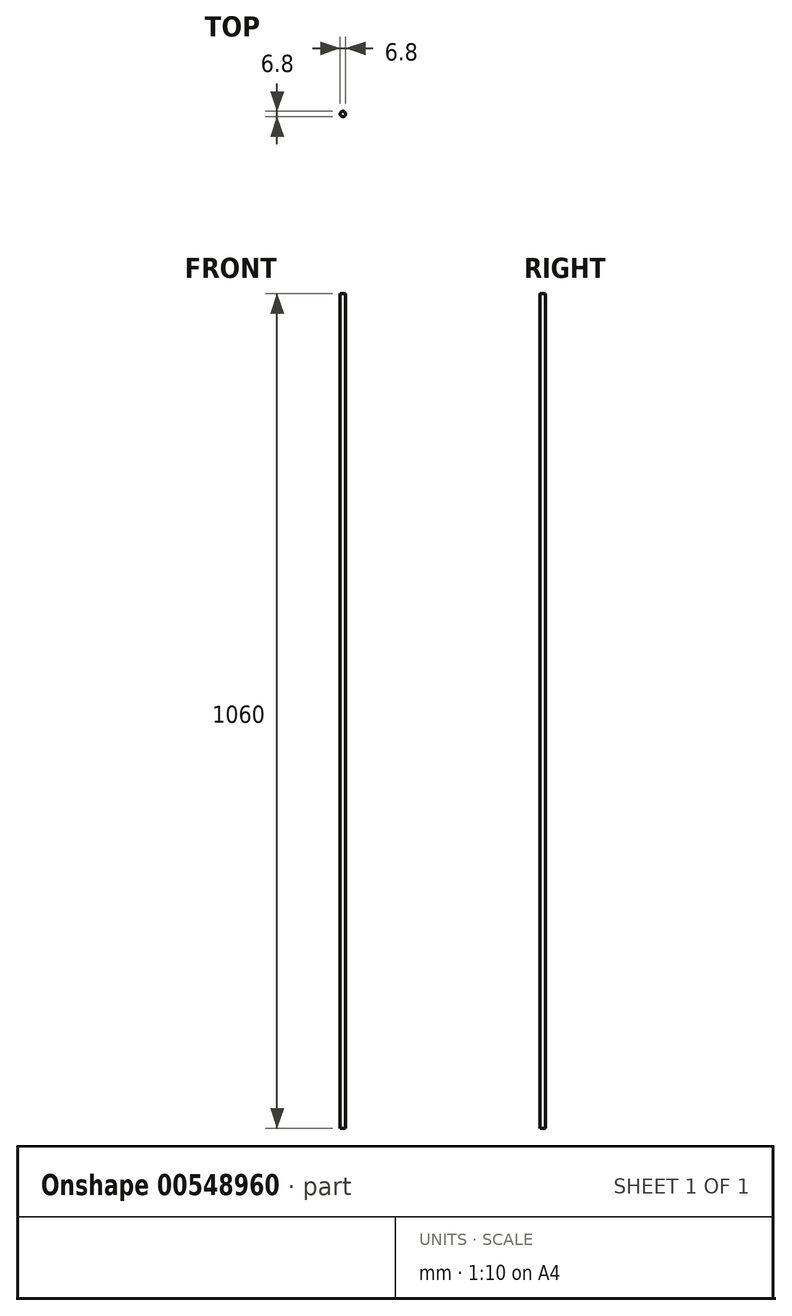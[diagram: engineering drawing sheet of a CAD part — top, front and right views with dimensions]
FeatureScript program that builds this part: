
annotation { "Feature Type Name" : "Feature", "Feature Type Description" : "" }
export const myFeature = defineFeature(function(context is Context, id is Id, definition is map)
    precondition{}
    {
        {
            var Q0;
            Q0=qCreatedBy(makeId("Top.planeOp"),FACE);
            var sketch = newSketch(context, id + "F0", { "sketchPlane" : qUnion([Q0])});
            skCircle(sketch, "E0", {"center": v(-29.73, 16.76) * mm, "radius": 3.4 * mm});
            skArc(sketch, "E1", {"start": v(-41.23, 8.76) * mm, "mid": v(-39.2, 10.8) * mm, "end": v(-37.83, 13.34) * mm});
            skArc(sketch, "E2", {"start": v(-37.83, 20.17) * mm, "mid": v(-39.2, 22.7) * mm, "end": v(-41.23, 24.76) * mm});
            skLineSegment(sketch, "E3", {"start": v(-37.68, 19.31) * mm, "end": v(-37.68, 14.2) * mm});
            skArc(sketch, "E4", {"start": v(-45.23, 10.76) * mm, "mid": v(-43.85, 8.52) * mm, "end": v(-41.23, 8.76) * mm});
            skArc(sketch, "E5", {"start": v(-41.23, 24.76) * mm, "mid": v(-43.85, 25) * mm, "end": v(-45.23, 22.76) * mm});
            skArc(sketch, "E6", {"start": v(-37.68, 19.31) * mm, "mid": v(-37.72, 19.75) * mm, "end": v(-37.83, 20.17) * mm});
            skArc(sketch, "E7", {"start": v(-37.83, 13.34) * mm, "mid": v(-37.72, 13.76) * mm, "end": v(-37.68, 14.2) * mm});
            skLineSegment(sketch, "E8", {"start": v(-47.25, 32.96) * mm, "end": v(-47.25, 30.28) * mm});
            skLineSegment(sketch, "E9", {"start": v(-43.16, 34.37) * mm, "end": v(-42.46, 35.08) * mm});
            skLineSegment(sketch, "E10", {"start": v(-42.46, 35.08) * mm, "end": v(-41.04, 33.66) * mm});
            skLineSegment(sketch, "E11", {"start": v(-41.04, 33.66) * mm, "end": v(-41.75, 32.96) * mm});
            skLineSegment(sketch, "E12", {"start": v(-41.75, 30.28) * mm, "end": v(-41.04, 29.58) * mm});
            skLineSegment(sketch, "E13", {"start": v(-41.04, 29.58) * mm, "end": v(-42.46, 28.16) * mm});
            skLineSegment(sketch, "E14", {"start": v(-42.46, 28.16) * mm, "end": v(-43.16, 28.87) * mm});
            skLineSegment(sketch, "E15", {"start": v(-47.25, 32.96) * mm, "end": v(-47.96, 33.66) * mm});
            skLineSegment(sketch, "E16", {"start": v(-47.96, 33.66) * mm, "end": v(-46.54, 35.08) * mm});
            skLineSegment(sketch, "E17", {"start": v(-46.54, 35.08) * mm, "end": v(-45.83, 34.37) * mm});
            skLineSegment(sketch, "E18", {"start": v(-45.83, 28.87) * mm, "end": v(-43.16, 28.87) * mm});
            skLineSegment(sketch, "E19", {"start": v(-45.83, 28.87) * mm, "end": v(-46.54, 28.16) * mm});
            skLineSegment(sketch, "E20", {"start": v(-46.54, 28.16) * mm, "end": v(-47.96, 29.58) * mm});
            skLineSegment(sketch, "E21", {"start": v(-47.96, 29.58) * mm, "end": v(-47.25, 30.28) * mm});
            skLineSegment(sketch, "E22", {"start": v(-43.16, 34.37) * mm, "end": v(-45.83, 34.37) * mm});
            skLineSegment(sketch, "E23", {"start": v(-41.75, 30.28) * mm, "end": v(-41.75, 32.96) * mm});
            skLineSegment(sketch, "E24", {"start": v(-45.23, 10.76) * mm, "end": v(-45.23, 12.06) * mm});
            skArc(sketch, "E25", {"start": v(-45.23, 12.06) * mm, "mid": v(-45.38, 12.4) * mm, "end": v(-45.73, 12.56) * mm});
            skLineSegment(sketch, "E26", {"start": v(-45.73, 12.56) * mm, "end": v(-47.23, 12.56) * mm});
            skArc(sketch, "E27", {"start": v(-47.23, 12.56) * mm, "mid": v(-49, 11.82) * mm, "end": v(-49.73, 10.06) * mm});
            skLineSegment(sketch, "E28", {"start": v(-49.73, 10.06) * mm, "end": v(-49.73, -0.74) * mm});
            skArc(sketch, "E29", {"start": v(-49.73, -0.74) * mm, "mid": v(-49, -2.51) * mm, "end": v(-47.23, -3.24) * mm});
            skArc(sketch, "E30", {"start": v(-12.23, -3.24) * mm, "mid": v(-10.46, -2.51) * mm, "end": v(-9.73, -0.74) * mm});
            skArc(sketch, "E31", {"start": v(-9.73, 34.26) * mm, "mid": v(-10.46, 36.02) * mm, "end": v(-12.23, 36.76) * mm});
            skArc(sketch, "E32", {"start": v(-47.23, 36.76) * mm, "mid": v(-49, 36.02) * mm, "end": v(-49.73, 34.26) * mm});
            skLineSegment(sketch, "E33", {"start": v(-49.73, 34.26) * mm, "end": v(-49.73, 23.46) * mm});
            skArc(sketch, "E34", {"start": v(-49.73, 23.46) * mm, "mid": v(-49, 21.69) * mm, "end": v(-47.23, 20.96) * mm});
            skLineSegment(sketch, "E35", {"start": v(-47.23, 20.96) * mm, "end": v(-45.73, 20.96) * mm});
            skArc(sketch, "E36", {"start": v(-45.73, 20.96) * mm, "mid": v(-45.38, 21.1) * mm, "end": v(-45.23, 21.46) * mm});
            skLineSegment(sketch, "E37", {"start": v(-45.23, 21.46) * mm, "end": v(-45.23, 22.76) * mm});
            skArc(sketch, "E38", {"start": v(-21.73, 5.26) * mm, "mid": v(-23.78, 7.29) * mm, "end": v(-26.32, 8.66) * mm});
            skArc(sketch, "E39", {"start": v(-33.14, 8.66) * mm, "mid": v(-35.68, 7.29) * mm, "end": v(-37.73, 5.26) * mm});
            skLineSegment(sketch, "E40", {"start": v(-32.29, 8.8) * mm, "end": v(-27.17, 8.8) * mm});
            skArc(sketch, "E41", {"start": v(-23.73, 1.26) * mm, "mid": v(-21.5, 2.64) * mm, "end": v(-21.73, 5.26) * mm});
            skArc(sketch, "E42", {"start": v(-37.73, 5.26) * mm, "mid": v(-37.97, 2.64) * mm, "end": v(-35.73, 1.26) * mm});
            skArc(sketch, "E43", {"start": v(-32.29, 8.8) * mm, "mid": v(-32.72, 8.77) * mm, "end": v(-33.14, 8.66) * mm});
            skArc(sketch, "E44", {"start": v(-26.32, 8.66) * mm, "mid": v(-26.74, 8.77) * mm, "end": v(-27.17, 8.8) * mm});
            skLineSegment(sketch, "E45", {"start": v(-23.73, 1.26) * mm, "end": v(-25.03, 1.26) * mm});
            skArc(sketch, "E46", {"start": v(-25.03, 1.26) * mm, "mid": v(-25.38, 1.1) * mm, "end": v(-25.53, 0.76) * mm});
            skLineSegment(sketch, "E47", {"start": v(-25.53, 0.76) * mm, "end": v(-25.53, -0.74) * mm});
            skArc(sketch, "E48", {"start": v(-25.53, -0.74) * mm, "mid": v(-24.8, -2.51) * mm, "end": v(-23.03, -3.24) * mm});
            skLineSegment(sketch, "E49", {"start": v(-23.03, -3.24) * mm, "end": v(-12.23, -3.24) * mm});
            skLineSegment(sketch, "E50", {"start": v(-47.23, -3.24) * mm, "end": v(-36.43, -3.24) * mm});
            skArc(sketch, "E51", {"start": v(-36.43, -3.24) * mm, "mid": v(-34.66, -2.51) * mm, "end": v(-33.93, -0.74) * mm});
            skLineSegment(sketch, "E52", {"start": v(-33.93, -0.74) * mm, "end": v(-33.93, 0.76) * mm});
            skArc(sketch, "E53", {"start": v(-33.93, 0.76) * mm, "mid": v(-34.08, 1.1) * mm, "end": v(-34.43, 1.26) * mm});
            skLineSegment(sketch, "E54", {"start": v(-34.43, 1.26) * mm, "end": v(-35.73, 1.26) * mm});
            skArc(sketch, "E55", {"start": v(-18.23, 24.76) * mm, "mid": v(-20.26, 22.7) * mm, "end": v(-21.63, 20.17) * mm});
            skArc(sketch, "E56", {"start": v(-21.63, 13.34) * mm, "mid": v(-20.26, 10.8) * mm, "end": v(-18.23, 8.76) * mm});
            skLineSegment(sketch, "E57", {"start": v(-21.78, 14.2) * mm, "end": v(-21.78, 19.31) * mm});
            skArc(sketch, "E58", {"start": v(-14.23, 22.76) * mm, "mid": v(-15.61, 25) * mm, "end": v(-18.23, 24.76) * mm});
            skArc(sketch, "E59", {"start": v(-18.23, 8.76) * mm, "mid": v(-15.61, 8.52) * mm, "end": v(-14.23, 10.76) * mm});
            skArc(sketch, "E60", {"start": v(-21.78, 14.2) * mm, "mid": v(-21.74, 13.76) * mm, "end": v(-21.63, 13.34) * mm});
            skArc(sketch, "E61", {"start": v(-21.63, 20.17) * mm, "mid": v(-21.74, 19.75) * mm, "end": v(-21.78, 19.31) * mm});
            skLineSegment(sketch, "E62", {"start": v(-14.23, 22.76) * mm, "end": v(-14.23, 21.46) * mm});
            skArc(sketch, "E63", {"start": v(-14.23, 21.46) * mm, "mid": v(-14.08, 21.1) * mm, "end": v(-13.73, 20.96) * mm});
            skLineSegment(sketch, "E64", {"start": v(-13.73, 20.96) * mm, "end": v(-12.23, 20.96) * mm});
            skArc(sketch, "E65", {"start": v(-12.23, 20.96) * mm, "mid": v(-10.46, 21.69) * mm, "end": v(-9.73, 23.46) * mm});
            skLineSegment(sketch, "E66", {"start": v(-9.73, 23.46) * mm, "end": v(-9.73, 34.26) * mm});
            skLineSegment(sketch, "E67", {"start": v(-9.73, -0.74) * mm, "end": v(-9.73, 10.06) * mm});
            skArc(sketch, "E68", {"start": v(-9.73, 10.06) * mm, "mid": v(-10.46, 11.82) * mm, "end": v(-12.23, 12.56) * mm});
            skLineSegment(sketch, "E69", {"start": v(-12.23, 12.56) * mm, "end": v(-13.73, 12.56) * mm});
            skArc(sketch, "E70", {"start": v(-13.73, 12.56) * mm, "mid": v(-14.08, 12.4) * mm, "end": v(-14.23, 12.06) * mm});
            skLineSegment(sketch, "E71", {"start": v(-14.23, 12.06) * mm, "end": v(-14.23, 10.76) * mm});
            skArc(sketch, "E72", {"start": v(-37.73, 28.26) * mm, "mid": v(-35.68, 26.22) * mm, "end": v(-33.14, 24.86) * mm});
            skArc(sketch, "E73", {"start": v(-26.32, 24.86) * mm, "mid": v(-23.78, 26.22) * mm, "end": v(-21.73, 28.26) * mm});
            skLineSegment(sketch, "E74", {"start": v(-27.17, 24.7) * mm, "end": v(-32.29, 24.7) * mm});
            skArc(sketch, "E75", {"start": v(-35.73, 32.26) * mm, "mid": v(-37.97, 30.87) * mm, "end": v(-37.73, 28.26) * mm});
            skArc(sketch, "E76", {"start": v(-21.73, 28.26) * mm, "mid": v(-21.5, 30.87) * mm, "end": v(-23.73, 32.26) * mm});
            skArc(sketch, "E77", {"start": v(-27.17, 24.7) * mm, "mid": v(-26.74, 24.74) * mm, "end": v(-26.32, 24.86) * mm});
            skArc(sketch, "E78", {"start": v(-33.14, 24.86) * mm, "mid": v(-32.72, 24.74) * mm, "end": v(-32.29, 24.7) * mm});
            skLineSegment(sketch, "E79", {"start": v(-35.73, 32.26) * mm, "end": v(-34.43, 32.26) * mm});
            skArc(sketch, "E80", {"start": v(-34.43, 32.26) * mm, "mid": v(-34.08, 32.4) * mm, "end": v(-33.93, 32.76) * mm});
            skLineSegment(sketch, "E81", {"start": v(-33.93, 32.76) * mm, "end": v(-33.93, 34.26) * mm});
            skArc(sketch, "E82", {"start": v(-33.93, 34.26) * mm, "mid": v(-34.66, 36.02) * mm, "end": v(-36.43, 36.76) * mm});
            skLineSegment(sketch, "E83", {"start": v(-36.43, 36.76) * mm, "end": v(-47.23, 36.76) * mm});
            skLineSegment(sketch, "E84", {"start": v(-12.23, 36.76) * mm, "end": v(-23.03, 36.76) * mm});
            skArc(sketch, "E85", {"start": v(-23.03, 36.76) * mm, "mid": v(-24.8, 36.02) * mm, "end": v(-25.53, 34.26) * mm});
            skLineSegment(sketch, "E86", {"start": v(-25.53, 34.26) * mm, "end": v(-25.53, 32.76) * mm});
            skArc(sketch, "E87", {"start": v(-25.53, 32.76) * mm, "mid": v(-25.38, 32.4) * mm, "end": v(-25.03, 32.26) * mm});
            skLineSegment(sketch, "E88", {"start": v(-25.03, 32.26) * mm, "end": v(-23.73, 32.26) * mm});
            skLineSegment(sketch, "E89", {"start": v(-45.93, -0.76) * mm, "end": v(-43.26, -0.76) * mm});
            skLineSegment(sketch, "E90", {"start": v(-47.34, 3.32) * mm, "end": v(-48.05, 4.03) * mm});
            skLineSegment(sketch, "E91", {"start": v(-48.05, 4.03) * mm, "end": v(-46.64, 5.44) * mm});
            skLineSegment(sketch, "E92", {"start": v(-46.64, 5.44) * mm, "end": v(-45.93, 4.74) * mm});
            skLineSegment(sketch, "E93", {"start": v(-43.26, 4.74) * mm, "end": v(-42.55, 5.44) * mm});
            skLineSegment(sketch, "E94", {"start": v(-42.55, 5.44) * mm, "end": v(-41.14, 4.03) * mm});
            skLineSegment(sketch, "E95", {"start": v(-41.14, 4.03) * mm, "end": v(-41.84, 3.32) * mm});
            skLineSegment(sketch, "E96", {"start": v(-45.93, -0.76) * mm, "end": v(-46.64, -1.47) * mm});
            skLineSegment(sketch, "E97", {"start": v(-46.64, -1.47) * mm, "end": v(-48.05, -0.06) * mm});
            skLineSegment(sketch, "E98", {"start": v(-48.05, -0.06) * mm, "end": v(-47.34, 0.65) * mm});
            skLineSegment(sketch, "E99", {"start": v(-41.84, 0.65) * mm, "end": v(-41.84, 3.32) * mm});
            skLineSegment(sketch, "E100", {"start": v(-41.84, 0.65) * mm, "end": v(-41.14, -0.06) * mm});
            skLineSegment(sketch, "E101", {"start": v(-41.14, -0.06) * mm, "end": v(-42.55, -1.47) * mm});
            skLineSegment(sketch, "E102", {"start": v(-42.55, -1.47) * mm, "end": v(-43.26, -0.76) * mm});
            skLineSegment(sketch, "E103", {"start": v(-47.34, 3.32) * mm, "end": v(-47.34, 0.65) * mm});
            skLineSegment(sketch, "E104", {"start": v(-43.26, 4.74) * mm, "end": v(-45.93, 4.74) * mm});
            skLineSegment(sketch, "E105", {"start": v(-12.2, 0.55) * mm, "end": v(-12.2, 3.23) * mm});
            skLineSegment(sketch, "E106", {"start": v(-16.3, -0.86) * mm, "end": v(-17, -1.57) * mm});
            skLineSegment(sketch, "E107", {"start": v(-17, -1.57) * mm, "end": v(-18.42, -0.15) * mm});
            skLineSegment(sketch, "E108", {"start": v(-18.42, -0.15) * mm, "end": v(-17.7, 0.55) * mm});
            skLineSegment(sketch, "E109", {"start": v(-17.7, 3.23) * mm, "end": v(-18.42, 3.93) * mm});
            skLineSegment(sketch, "E110", {"start": v(-18.42, 3.93) * mm, "end": v(-17, 5.35) * mm});
            skLineSegment(sketch, "E111", {"start": v(-17, 5.35) * mm, "end": v(-16.3, 4.64) * mm});
            skLineSegment(sketch, "E112", {"start": v(-12.2, 0.55) * mm, "end": v(-11.5, -0.15) * mm});
            skLineSegment(sketch, "E113", {"start": v(-11.5, -0.15) * mm, "end": v(-12.92, -1.57) * mm});
            skLineSegment(sketch, "E114", {"start": v(-12.92, -1.57) * mm, "end": v(-13.62, -0.86) * mm});
            skLineSegment(sketch, "E115", {"start": v(-13.62, 4.64) * mm, "end": v(-16.3, 4.64) * mm});
            skLineSegment(sketch, "E116", {"start": v(-13.62, 4.64) * mm, "end": v(-12.92, 5.35) * mm});
            skLineSegment(sketch, "E117", {"start": v(-12.92, 5.35) * mm, "end": v(-11.5, 3.93) * mm});
            skLineSegment(sketch, "E118", {"start": v(-11.5, 3.93) * mm, "end": v(-12.2, 3.23) * mm});
            skLineSegment(sketch, "E119", {"start": v(-16.3, -0.86) * mm, "end": v(-13.62, -0.86) * mm});
            skLineSegment(sketch, "E120", {"start": v(-17.7, 3.23) * mm, "end": v(-17.7, 0.55) * mm});
            skLineSegment(sketch, "E121", {"start": v(-13.53, 34.28) * mm, "end": v(-16.2, 34.28) * mm});
            skLineSegment(sketch, "E122", {"start": v(-12.11, 30.19) * mm, "end": v(-11.4, 29.48) * mm});
            skLineSegment(sketch, "E123", {"start": v(-11.4, 29.48) * mm, "end": v(-12.82, 28.07) * mm});
            skLineSegment(sketch, "E124", {"start": v(-12.82, 28.07) * mm, "end": v(-13.53, 28.78) * mm});
            skLineSegment(sketch, "E125", {"start": v(-16.2, 28.78) * mm, "end": v(-16.9, 28.07) * mm});
            skLineSegment(sketch, "E126", {"start": v(-16.9, 28.07) * mm, "end": v(-18.32, 29.48) * mm});
            skLineSegment(sketch, "E127", {"start": v(-18.32, 29.48) * mm, "end": v(-17.61, 30.19) * mm});
            skLineSegment(sketch, "E128", {"start": v(-13.53, 34.28) * mm, "end": v(-12.82, 34.98) * mm});
            skLineSegment(sketch, "E129", {"start": v(-12.82, 34.98) * mm, "end": v(-11.4, 33.57) * mm});
            skLineSegment(sketch, "E130", {"start": v(-11.4, 33.57) * mm, "end": v(-12.11, 32.86) * mm});
            skLineSegment(sketch, "E131", {"start": v(-17.61, 32.86) * mm, "end": v(-17.61, 30.19) * mm});
            skLineSegment(sketch, "E132", {"start": v(-17.61, 32.86) * mm, "end": v(-18.32, 33.57) * mm});
            skLineSegment(sketch, "E133", {"start": v(-18.32, 33.57) * mm, "end": v(-16.9, 34.98) * mm});
            skLineSegment(sketch, "E134", {"start": v(-16.9, 34.98) * mm, "end": v(-16.2, 34.28) * mm});
            skLineSegment(sketch, "E135", {"start": v(-12.11, 30.19) * mm, "end": v(-12.11, 32.86) * mm});
            skLineSegment(sketch, "E136", {"start": v(-16.2, 28.78) * mm, "end": v(-13.53, 28.78) * mm});
            skSolve(sketch);
        }
        {
            var Q0;
            Q0=makeQuery(id+"F0.imprint","IMPRINT",FACE,{"disambiguationData":[TD([[makeQuery(id+"F0.imprint","IMPRINT",EDGE,{"derivedFrom":sQuery(id+"F0.wireOp",EDGE,"E0")}),1.0]])]});
            extrude(context, id + "F1", {"entities" : qUnion([Q0]), "depth" : 1060 * mm, "offsetDistance" : 25 * mm});
        }
    });
